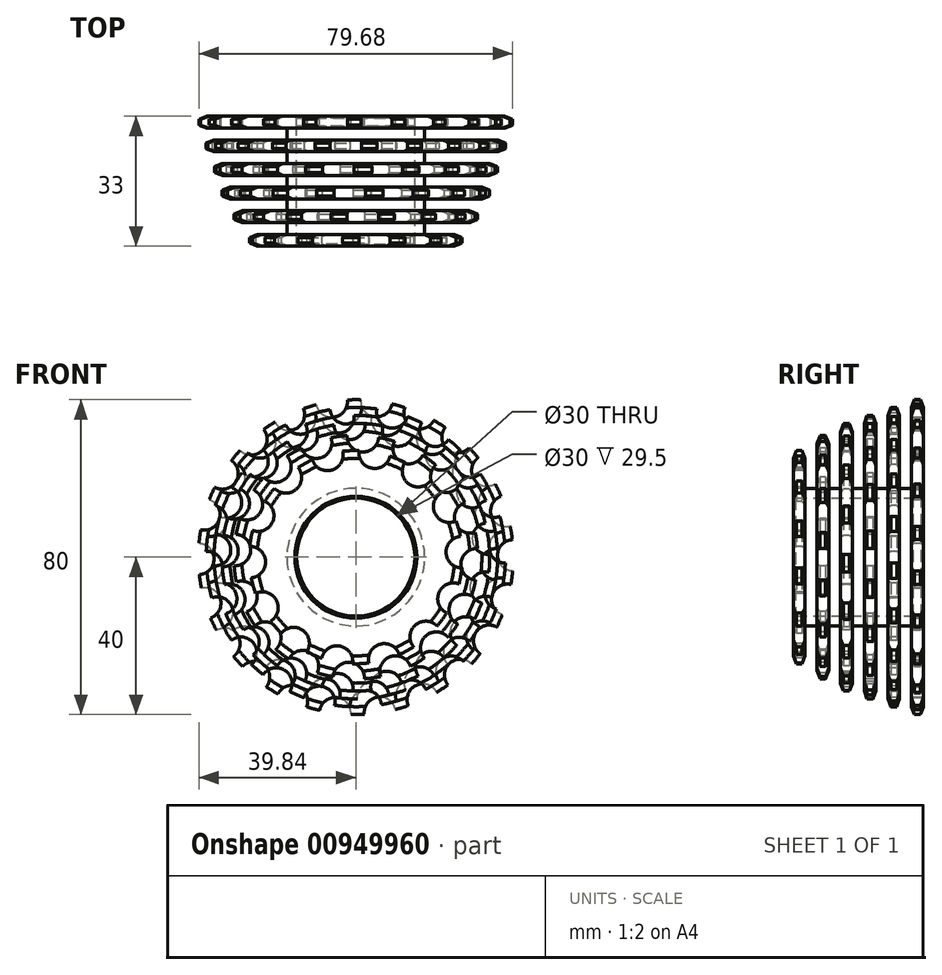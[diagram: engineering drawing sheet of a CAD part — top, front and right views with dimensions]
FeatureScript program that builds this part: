
annotation { "Feature Type Name" : "Feature", "Feature Type Description" : "" }
export const myFeature = defineFeature(function(context is Context, id is Id, definition is map)
    precondition{}
    {
        {
            var Q0;
            Q0=qCreatedBy(makeId("Front.planeOp"),FACE);
            var sketch = newSketch(context, id + "F0", { "sketchPlane" : qUnion([Q0])});
            skCircle(sketch, "E0", {"center": v(0, 0) * mm, "radius": 40 * mm});
            skCircle(sketch, "E1", {"center": v(-33.89, 21.25) * mm, "radius": 4 * mm});
            skCircle(sketch, "E2.1.0", {"center": v(-38.5, 10.85) * mm, "radius": 4 * mm});
            skCircle(sketch, "E2.2.0", {"center": v(-40, -0.44) * mm, "radius": 4 * mm});
            skCircle(sketch, "E2.3.0", {"center": v(-38.25, -11.7) * mm, "radius": 4 * mm});
            skCircle(sketch, "E2.4.0", {"center": v(-33.41, -22) * mm, "radius": 4 * mm});
            skCircle(sketch, "E2.5.0", {"center": v(-25.86, -30.52) * mm, "radius": 4 * mm});
            skCircle(sketch, "E2.6.0", {"center": v(-16.22, -36.57) * mm, "radius": 4 * mm});
            skCircle(sketch, "E2.7.0", {"center": v(-5.26, -39.65) * mm, "radius": 4 * mm});
            skCircle(sketch, "E2.8.0", {"center": v(6.13, -39.53) * mm, "radius": 4 * mm});
            skCircle(sketch, "E2.9.0", {"center": v(17.02, -36.2) * mm, "radius": 4 * mm});
            skCircle(sketch, "E2.10.0", {"center": v(26.53, -29.94) * mm, "radius": 4 * mm});
            skCircle(sketch, "E2.11.0", {"center": v(33.89, -21.25) * mm, "radius": 4 * mm});
            skCircle(sketch, "E2.12.0", {"center": v(38.5, -10.85) * mm, "radius": 4 * mm});
            skCircle(sketch, "E2.13.0", {"center": v(40, 0.44) * mm, "radius": 4 * mm});
            skCircle(sketch, "E2.14.0", {"center": v(38.25, 11.7) * mm, "radius": 4 * mm});
            skCircle(sketch, "E2.15.0", {"center": v(33.41, 22) * mm, "radius": 4 * mm});
            skCircle(sketch, "E2.16.0", {"center": v(25.86, 30.52) * mm, "radius": 4 * mm});
            skCircle(sketch, "E2.17.0", {"center": v(16.22, 36.57) * mm, "radius": 4 * mm});
            skCircle(sketch, "E2.18.0", {"center": v(5.26, 39.65) * mm, "radius": 4 * mm});
            skCircle(sketch, "E2.19.0", {"center": v(-6.13, 39.53) * mm, "radius": 4 * mm});
            skCircle(sketch, "E3", {"center": v(0, 0) * mm, "radius": 15 * mm});
            skCircle(sketch, "E4.1.20.0", {"center": v(-17.02, 36.2) * mm, "radius": 4 * mm});
            skCircle(sketch, "E4.1.21.0", {"center": v(-26.53, 29.94) * mm, "radius": 4 * mm});
            skSolve(sketch);
        }
        {
            var Q0;
            Q0=makeQuery(id+"F0.imprint","IMPRINT",FACE,{"disambiguationData":[TD([[makeQuery(id+"F0.imprint","IMPRINT",EDGE,{"derivedFrom":sQuery(id+"F0.wireOp",EDGE,"E0")}),1.0]])]});
            extrude(context, id + "F1", {"entities" : qUnion([Q0]), "depth" : 3 * mm, "offsetDistance" : 25 * mm});
        }
        {
            var Q0;
            {var subQ0=sQuery(id+"F0.wireOp",EDGE,"E0");Q0=makeQuery(id+"FjPS6zSCau8WYdw_1.boolean.opBoolean","SPLIT",EDGE,{"disambiguationData":[TD([makeQuery(id+"F1.opExtrude","SWEPT_FACE",FACE,{"disambiguationData":[OSD([subQ0])]}),makeQuery(id+"F1.opExtrude","CAP_FACE",FACE,{"disambiguationData":[OSD([subQ0])],"isStart":false}),makeQuery(id+"FjPS6zSCau8WYdw_1.opExtrude","SWEPT_FACE",FACE,{"disambiguationData":[OSD([sQuery(id+"FptURnvkRjZK9U8_1.wireOp",EDGE,"c81c12ed-b287-469f-bd1e-95274906ad68.5.0")])]}),makeQuery(id+"FjPS6zSCau8WYdw_1.opExtrude","SWEPT_FACE",FACE,{"disambiguationData":[OSD([sQuery(id+"FptURnvkRjZK9U8_1.wireOp",EDGE,"c81c12ed-b287-469f-bd1e-95274906ad68.6.0")])]})])],"derivedFrom":makeQuery(id+"F1.opExtrude","CAP_EDGE",EDGE,{"disambiguationData":[OSD([subQ0])],"isStart":false})});}
            chamfer(context, id + "F2", {"entities" : qUnion([Q0]), "chamferType" : ChamferType.TWO_OFFSETS, "width1" : 2 * mm, "oppositeDirection" : false, "width2" : 0.75 * mm, "tangentPropagation" : true});
        }
        {
            var Q0;
            {var subQ0=sQuery(id+"F0.wireOp",EDGE,"E0");Q0=makeQuery(id+"FjPS6zSCau8WYdw_1.boolean.opBoolean","SPLIT",EDGE,{"disambiguationData":[TD([makeQuery(id+"F1.opExtrude","SWEPT_FACE",FACE,{"disambiguationData":[OSD([subQ0])]}),makeQuery(id+"F1.opExtrude","CAP_FACE",FACE,{"disambiguationData":[OSD([subQ0])],"isStart":true}),makeQuery(id+"FjPS6zSCau8WYdw_1.opExtrude","SWEPT_FACE",FACE,{"disambiguationData":[OSD([sQuery(id+"FptURnvkRjZK9U8_1.wireOp",EDGE,"c81c12ed-b287-469f-bd1e-95274906ad68.21.0")])]}),makeQuery(id+"FjPS6zSCau8WYdw_1.opExtrude","SWEPT_FACE",FACE,{"disambiguationData":[OSD([sQuery(id+"FptURnvkRjZK9U8_1.wireOp",EDGE,"c81c12ed-b287-469f-bd1e-95274906ad68.22.0")])]})])],"derivedFrom":makeQuery(id+"F1.opExtrude","CAP_EDGE",EDGE,{"disambiguationData":[OSD([subQ0])],"isStart":true})});}
            chamfer(context, id + "F3", {"entities" : qUnion([Q0]), "chamferType" : ChamferType.TWO_OFFSETS, "width1" : 0.75 * mm, "oppositeDirection" : false, "width2" : 2 * mm, "tangentPropagation" : true});
        }
        {
            var Q0;
            Q0=makeQuery(id+"F1.opExtrude","CAP_EDGE",EDGE,{"disambiguationData":[OSD([sQuery(id+"F0.wireOp",EDGE,"E3")])],"isStart":false});
            var Q1;
            Q1=makeQuery(id+"F1.opExtrude","CAP_EDGE",EDGE,{"disambiguationData":[OSD([sQuery(id+"F0.wireOp",EDGE,"E3")])],"isStart":true});
            chamfer(context, id + "F4", {"entities" : qUnion([Q0, Q1]), "width" : 0.5 * mm, "tangentPropagation" : true});
        }
        {
            var Q0;
            Q0=makeQuery(id+"F1.opExtrude","CAP_FACE",FACE,{"disambiguationData":[OSD([sQuery(id+"F0.wireOp",EDGE,"E0"),sQuery(id+"F0.wireOp",EDGE,"E1"),sQuery(id+"F0.wireOp",EDGE,"E2.1.0"),sQuery(id+"F0.wireOp",EDGE,"E2.2.0"),sQuery(id+"F0.wireOp",EDGE,"E2.3.0"),sQuery(id+"F0.wireOp",EDGE,"E2.4.0"),sQuery(id+"F0.wireOp",EDGE,"E2.5.0"),sQuery(id+"F0.wireOp",EDGE,"E2.6.0"),sQuery(id+"F0.wireOp",EDGE,"E2.7.0"),sQuery(id+"F0.wireOp",EDGE,"E2.8.0"),sQuery(id+"F0.wireOp",EDGE,"E2.9.0"),sQuery(id+"F0.wireOp",EDGE,"E2.10.0"),sQuery(id+"F0.wireOp",EDGE,"E2.11.0"),sQuery(id+"F0.wireOp",EDGE,"E2.12.0"),sQuery(id+"F0.wireOp",EDGE,"E2.13.0"),sQuery(id+"F0.wireOp",EDGE,"E2.14.0"),sQuery(id+"F0.wireOp",EDGE,"E2.15.0"),sQuery(id+"F0.wireOp",EDGE,"E2.16.0"),sQuery(id+"F0.wireOp",EDGE,"E2.17.0"),sQuery(id+"F0.wireOp",EDGE,"E2.18.0"),sQuery(id+"F0.wireOp",EDGE,"E2.19.0"),sQuery(id+"F0.wireOp",EDGE,"E3"),sQuery(id+"F0.wireOp",EDGE,"E4.1.20.0"),sQuery(id+"F0.wireOp",EDGE,"E4.1.21.0")])],"isStart":false});
            var sketch = newSketch(context, id + "F5", { "sketchPlane" : qUnion([Q0])});
            skCircle(sketch, "E5", {"center": v(0, 0) * mm, "radius": 17.5 * mm});
            skSolve(sketch);
        }
        {
            var Q0;
            Q0 = qSketchRegion(id + "F5", true);
            extrude(context, id + "F6", {"entities" : qUnion([Q0]), "operationType" : NewBodyOperationType.ADD, "depth" : 3 * mm, "offsetDistance" : 25 * mm});
        }
        {
            var Q0;
            Q0=makeQuery(id+"F6.opExtrude","CAP_FACE",FACE,{"disambiguationData":[OSD([sQuery(id+"F5.wireOp",EDGE,"E5")])],"isStart":false});
            var sketch = newSketch(context, id + "F7", { "sketchPlane" : qUnion([Q0])});
            skCircle(sketch, "E6", {"center": v(0, 0) * mm, "radius": 38.02 * mm});
            skSolve(sketch);
        }
        {
            var Q0;
            Q0 = qSketchRegion(id + "F7", true);
            extrude(context, id + "F8", {"entities" : qUnion([Q0]), "operationType" : NewBodyOperationType.ADD, "depth" : 3 * mm, "offsetDistance" : 25 * mm});
        }
        {
            var Q0;
            Q0=makeQuery(id+"F8.opExtrude","CAP_EDGE",EDGE,{"disambiguationData":[OSD([sQuery(id+"F7.wireOp",EDGE,"E6")])],"isStart":false});
            var Q1;
            Q1=makeQuery(id+"F8.opExtrude","CAP_EDGE",EDGE,{"disambiguationData":[OSD([sQuery(id+"F7.wireOp",EDGE,"E6")])],"isStart":true});
            chamfer(context, id + "F9", {"entities" : qUnion([Q0, Q1]), "chamferType" : ChamferType.TWO_OFFSETS, "width1" : 2 * mm, "oppositeDirection" : false, "width2" : 0.75 * mm, "tangentPropagation" : true});
        }
        {
            var Q0;
            Q0=makeQuery(id+"F8.opExtrude","CAP_FACE",FACE,{"disambiguationData":[OSD([sQuery(id+"F7.wireOp",EDGE,"E6")])],"isStart":false});
            var sketch = newSketch(context, id + "F10", { "sketchPlane" : qUnion([Q0])});
            skCircle(sketch, "E7", {"center": v(-32.1, 20.2) * mm, "radius": 4 * mm});
            skCircle(sketch, "E8.1.0", {"center": v(-36.78, 9.29) * mm, "radius": 4 * mm});
            skCircle(sketch, "E8.2.0", {"center": v(-37.85, -2.53) * mm, "radius": 4 * mm});
            skCircle(sketch, "E8.3.0", {"center": v(-35.21, -14.1) * mm, "radius": 4 * mm});
            skCircle(sketch, "E8.4.0", {"center": v(-29.13, -24.3) * mm, "radius": 4 * mm});
            skCircle(sketch, "E8.5.0", {"center": v(-20.2, -32.1) * mm, "radius": 4 * mm});
            skCircle(sketch, "E8.6.0", {"center": v(-9.29, -36.78) * mm, "radius": 4 * mm});
            skCircle(sketch, "E8.7.0", {"center": v(2.53, -37.85) * mm, "radius": 4 * mm});
            skCircle(sketch, "E8.8.0", {"center": v(14.1, -35.21) * mm, "radius": 4 * mm});
            skCircle(sketch, "E8.9.0", {"center": v(24.3, -29.13) * mm, "radius": 4 * mm});
            skCircle(sketch, "E8.10.0", {"center": v(32.1, -20.2) * mm, "radius": 4 * mm});
            skCircle(sketch, "E8.11.0", {"center": v(36.78, -9.29) * mm, "radius": 4 * mm});
            skCircle(sketch, "E8.12.0", {"center": v(37.85, 2.53) * mm, "radius": 4 * mm});
            skCircle(sketch, "E8.13.0", {"center": v(35.21, 14.1) * mm, "radius": 4 * mm});
            skCircle(sketch, "E8.14.0", {"center": v(29.13, 24.3) * mm, "radius": 4 * mm});
            skCircle(sketch, "E8.15.0", {"center": v(20.2, 32.1) * mm, "radius": 4 * mm});
            skCircle(sketch, "E8.16.0", {"center": v(9.29, 36.78) * mm, "radius": 4 * mm});
            skCircle(sketch, "E8.17.0", {"center": v(-2.53, 37.85) * mm, "radius": 4 * mm});
            skCircle(sketch, "E8.18.0", {"center": v(-14.1, 35.21) * mm, "radius": 4 * mm});
            skCircle(sketch, "E8.19.0", {"center": v(-24.3, 29.13) * mm, "radius": 4 * mm});
            skPoint(sketch, "E8.center", {"position": v(0, 0) * mm});
            skSolve(sketch);
        }
        {
            var Q0;
            Q0 = qSketchRegion(id + "F10", true);
            extrude(context, id + "F11", {"entities" : qUnion([Q0]), "operationType" : NewBodyOperationType.REMOVE, "oppositeDirection" : true, "depth" : 3 * mm, "offsetDistance" : 25 * mm});
        }
        {
            var Q0;
            Q0=makeQuery(id+"F8.opExtrude","CAP_FACE",FACE,{"disambiguationData":[OSD([sQuery(id+"F7.wireOp",EDGE,"E6")])],"isStart":false});
            var sketch = newSketch(context, id + "F12", { "sketchPlane" : qUnion([Q0])});
            skCircle(sketch, "E9", {"center": v(0, 0) * mm, "radius": 17.5 * mm});
            skSolve(sketch);
        }
        {
            var Q0;
            Q0 = qSketchRegion(id + "F12", true);
            extrude(context, id + "F13", {"entities" : qUnion([Q0]), "operationType" : NewBodyOperationType.ADD, "depth" : 3 * mm, "offsetDistance" : 25 * mm});
        }
        {
            var Q0;
            Q0=makeQuery(id+"F13.opExtrude","CAP_FACE",FACE,{"disambiguationData":[OSD([sQuery(id+"F12.wireOp",EDGE,"E9")])],"isStart":false});
            var sketch = newSketch(context, id + "F14", { "sketchPlane" : qUnion([Q0])});
            skCircle(sketch, "E10", {"center": v(0, 0) * mm, "radius": 36 * mm});
            skSolve(sketch);
        }
        {
            var Q0;
            Q0 = qSketchRegion(id + "F14", true);
            extrude(context, id + "F15", {"entities" : qUnion([Q0]), "operationType" : NewBodyOperationType.ADD, "depth" : 3 * mm, "offsetDistance" : 25 * mm});
        }
        {
            var Q0;
            Q0=makeQuery(id+"F15.opExtrude","CAP_FACE",FACE,{"disambiguationData":[OSD([sQuery(id+"F14.wireOp",EDGE,"E10")])],"isStart":false});
            var Q1;
            Q1=makeQuery(id+"F15.opExtrude","CAP_EDGE",EDGE,{"disambiguationData":[OSD([sQuery(id+"F14.wireOp",EDGE,"E10")])],"isStart":true});
            chamfer(context, id + "F16", {"entities" : qUnion([Q0, Q1]), "chamferType" : ChamferType.TWO_OFFSETS, "width1" : 2 * mm, "oppositeDirection" : false, "width2" : .75 * mm, "tangentPropagation" : true});
        }
        {
            var Q0;
            Q0=makeQuery(id+"F15.opExtrude","CAP_FACE",FACE,{"disambiguationData":[OSD([sQuery(id+"F14.wireOp",EDGE,"E10")])],"isStart":false});
            var sketch = newSketch(context, id + "F17", { "sketchPlane" : qUnion([Q0])});
            skCircle(sketch, "E11", {"center": v(-26.24, 24.36) * mm, "radius": 4 * mm});
            skCircle(sketch, "E12.1.0", {"center": v(-32.99, 13.92) * mm, "radius": 4 * mm});
            skCircle(sketch, "E12.2.0", {"center": v(-35.76, 1.8) * mm, "radius": 4 * mm});
            skCircle(sketch, "E12.3.0", {"center": v(-34.22, -10.54) * mm, "radius": 4 * mm});
            skCircle(sketch, "E12.4.0", {"center": v(-28.55, -21.6) * mm, "radius": 4 * mm});
            skCircle(sketch, "E12.5.0", {"center": v(-19.43, -30.07) * mm, "radius": 4 * mm});
            skCircle(sketch, "E12.6.0", {"center": v(-7.98, -34.9) * mm, "radius": 4 * mm});
            skCircle(sketch, "E12.7.0", {"center": v(4.44, -35.53) * mm, "radius": 4 * mm});
            skCircle(sketch, "E12.8.0", {"center": v(16.32, -31.87) * mm, "radius": 4 * mm});
            skCircle(sketch, "E12.9.0", {"center": v(26.24, -24.36) * mm, "radius": 4 * mm});
            skCircle(sketch, "E12.10.0", {"center": v(32.99, -13.92) * mm, "radius": 4 * mm});
            skCircle(sketch, "E12.11.0", {"center": v(35.76, -1.8) * mm, "radius": 4 * mm});
            skCircle(sketch, "E12.12.0", {"center": v(34.22, 10.54) * mm, "radius": 4 * mm});
            skCircle(sketch, "E12.13.0", {"center": v(28.55, 21.6) * mm, "radius": 4 * mm});
            skCircle(sketch, "E12.14.0", {"center": v(19.43, 30.07) * mm, "radius": 4 * mm});
            skCircle(sketch, "E12.15.0", {"center": v(7.98, 34.9) * mm, "radius": 4 * mm});
            skCircle(sketch, "E12.16.0", {"center": v(-4.44, 35.53) * mm, "radius": 4 * mm});
            skCircle(sketch, "E12.17.0", {"center": v(-16.32, 31.87) * mm, "radius": 4 * mm});
            skPoint(sketch, "E12.center", {"position": v(0, 0) * mm});
            skSolve(sketch);
        }
        {
            var Q0;
            Q0 = qSketchRegion(id + "F17", true);
            extrude(context, id + "F18", {"entities" : qUnion([Q0]), "operationType" : NewBodyOperationType.REMOVE, "oppositeDirection" : true, "depth" : 3 * mm, "offsetDistance" : 25 * mm});
        }
        {
            var Q0;
            Q0=makeQuery(id+"F15.opExtrude","CAP_FACE",FACE,{"disambiguationData":[OSD([sQuery(id+"F14.wireOp",EDGE,"E10")])],"isStart":false});
            var sketch = newSketch(context, id + "F19", { "sketchPlane" : qUnion([Q0])});
            skCircle(sketch, "E13", {"center": v(0, 0) * mm, "radius": 17.5 * mm});
            skSolve(sketch);
        }
        {
            var Q0;
            Q0 = qSketchRegion(id + "F19", true);
            extrude(context, id + "F20", {"entities" : qUnion([Q0]), "operationType" : NewBodyOperationType.ADD, "depth" : 3 * mm, "offsetDistance" : 25 * mm});
        }
        {
            var Q0;
            Q0=makeQuery(id+"F20.opExtrude","CAP_FACE",FACE,{"disambiguationData":[OSD([sQuery(id+"F19.wireOp",EDGE,"E13")])],"isStart":false});
            var sketch = newSketch(context, id + "F21", { "sketchPlane" : qUnion([Q0])});
            skCircle(sketch, "E14", {"center": v(0, 0) * mm, "radius": 34.02 * mm});
            skSolve(sketch);
        }
        {
            var Q0;
            Q0 = qSketchRegion(id + "F21", true);
            extrude(context, id + "F22", {"entities" : qUnion([Q0]), "operationType" : NewBodyOperationType.ADD, "depth" : 3 * mm, "offsetDistance" : 25 * mm});
        }
        {
            var Q0;
            Q0=makeQuery(id+"F22.opExtrude","CAP_FACE",FACE,{"disambiguationData":[OSD([sQuery(id+"F21.wireOp",EDGE,"E14")])],"isStart":false});
            var Q1;
            Q1=makeQuery(id+"F22.opExtrude","CAP_EDGE",EDGE,{"disambiguationData":[OSD([sQuery(id+"F21.wireOp",EDGE,"E14")])],"isStart":true});
            chamfer(context, id + "F23", {"entities" : qUnion([Q0, Q1]), "chamferType" : ChamferType.TWO_OFFSETS, "width1" : 2 * mm, "oppositeDirection" : false, "width2" : 0.75 * mm, "tangentPropagation" : true});
        }
        {
            var Q0;
            Q0=makeQuery(id+"F22.opExtrude","CAP_FACE",FACE,{"disambiguationData":[OSD([sQuery(id+"F21.wireOp",EDGE,"E14")])],"isStart":false});
            var sketch = newSketch(context, id + "F24", { "sketchPlane" : qUnion([Q0])});
            skCircle(sketch, "E15", {"center": v(-23.99, 23.95) * mm, "radius": 4 * mm});
            skCircle(sketch, "E16.1.0", {"center": v(-31.02, 13.67) * mm, "radius": 4 * mm});
            skCircle(sketch, "E16.2.0", {"center": v(-33.86, 1.54) * mm, "radius": 4 * mm});
            skCircle(sketch, "E16.3.0", {"center": v(-32.13, -10.8) * mm, "radius": 4 * mm});
            skCircle(sketch, "E16.4.0", {"center": v(-26.06, -21.67) * mm, "radius": 4 * mm});
            skCircle(sketch, "E16.5.0", {"center": v(-16.47, -29.62) * mm, "radius": 4 * mm});
            skCircle(sketch, "E16.6.0", {"center": v(-4.66, -33.57) * mm, "radius": 4 * mm});
            skCircle(sketch, "E16.7.0", {"center": v(7.78, -33) * mm, "radius": 4 * mm});
            skCircle(sketch, "E16.8.0", {"center": v(19.18, -27.95) * mm, "radius": 4 * mm});
            skCircle(sketch, "E16.9.0", {"center": v(27.98, -19.14) * mm, "radius": 4 * mm});
            skCircle(sketch, "E16.10.0", {"center": v(33, -7.74) * mm, "radius": 4 * mm});
            skCircle(sketch, "E16.11.0", {"center": v(33.57, 4.7) * mm, "radius": 4 * mm});
            skCircle(sketch, "E16.12.0", {"center": v(29.6, 16.52) * mm, "radius": 4 * mm});
            skCircle(sketch, "E16.13.0", {"center": v(21.64, 26.1) * mm, "radius": 4 * mm});
            skCircle(sketch, "E16.14.0", {"center": v(10.75, 32.15) * mm, "radius": 4 * mm});
            skCircle(sketch, "E16.15.0", {"center": v(-1.59, 33.86) * mm, "radius": 4 * mm});
            skCircle(sketch, "E16.16.0", {"center": v(-13.71, 31) * mm, "radius": 4 * mm});
            skPoint(sketch, "E16.center", {"position": v(0, 0) * mm});
            skSolve(sketch);
        }
        {
            var Q0;
            Q0 = qSketchRegion(id + "F24", true);
            extrude(context, id + "F25", {"entities" : qUnion([Q0]), "operationType" : NewBodyOperationType.REMOVE, "oppositeDirection" : true, "depth" : 3 * mm, "offsetDistance" : 25 * mm});
        }
        {
            var Q0;
            Q0=makeQuery(id+"F22.opExtrude","CAP_FACE",FACE,{"disambiguationData":[OSD([sQuery(id+"F21.wireOp",EDGE,"E14")])],"isStart":false});
            var sketch = newSketch(context, id + "F26", { "sketchPlane" : qUnion([Q0])});
            skCircle(sketch, "E17", {"center": v(0, 0) * mm, "radius": 17.5 * mm});
            skSolve(sketch);
        }
        {
            var Q0;
            Q0 = qSketchRegion(id + "F26", true);
            extrude(context, id + "F27", {"entities" : qUnion([Q0]), "operationType" : NewBodyOperationType.ADD, "depth" : 3 * mm, "offsetDistance" : 25 * mm});
        }
        {
            var Q0;
            Q0=makeQuery(id+"F27.opExtrude","CAP_FACE",FACE,{"disambiguationData":[OSD([sQuery(id+"F26.wireOp",EDGE,"E17")])],"isStart":false});
            var sketch = newSketch(context, id + "F28", { "sketchPlane" : qUnion([Q0])});
            skCircle(sketch, "E18", {"center": v(0, 0) * mm, "radius": 30.98 * mm});
            skSolve(sketch);
        }
        {
            var Q0;
            Q0 = qSketchRegion(id + "F28", true);
            extrude(context, id + "F29", {"entities" : qUnion([Q0]), "operationType" : NewBodyOperationType.ADD, "depth" : 3 * mm, "offsetDistance" : 25 * mm});
        }
        {
            var Q0;
            Q0=makeQuery(id+"F29.opExtrude","CAP_EDGE",EDGE,{"disambiguationData":[OSD([sQuery(id+"F28.wireOp",EDGE,"E18")])],"isStart":false});
            var Q1;
            Q1=makeQuery(id+"F29.opExtrude","CAP_EDGE",EDGE,{"disambiguationData":[OSD([sQuery(id+"F28.wireOp",EDGE,"E18")])],"isStart":true});
            chamfer(context, id + "F30", {"entities" : qUnion([Q0, Q1]), "chamferType" : ChamferType.TWO_OFFSETS, "width1" : 2 * mm, "oppositeDirection" : false, "width2" : 0.8 * mm, "tangentPropagation" : true});
        }
        {
            var Q0;
            Q0=makeQuery(id+"F29.opExtrude","CAP_FACE",FACE,{"disambiguationData":[OSD([sQuery(id+"F28.wireOp",EDGE,"E18")])],"isStart":false});
            var sketch = newSketch(context, id + "F31", { "sketchPlane" : qUnion([Q0])});
            skCircle(sketch, "E19", {"center": v(-20.44, 23) * mm, "radius": 4 * mm});
            skCircle(sketch, "E20.1.0", {"center": v(-27.68, 13.42) * mm, "radius": 4 * mm});
            skCircle(sketch, "E20.2.0", {"center": v(-30.71, 1.8) * mm, "radius": 4 * mm});
            skCircle(sketch, "E20.3.0", {"center": v(-29.07, -10.08) * mm, "radius": 4 * mm});
            skCircle(sketch, "E20.4.0", {"center": v(-23, -20.44) * mm, "radius": 4 * mm});
            skCircle(sketch, "E20.5.0", {"center": v(-13.42, -27.68) * mm, "radius": 4 * mm});
            skCircle(sketch, "E20.6.0", {"center": v(-1.8, -30.71) * mm, "radius": 4 * mm});
            skCircle(sketch, "E20.7.0", {"center": v(10.08, -29.07) * mm, "radius": 4 * mm});
            skCircle(sketch, "E20.8.0", {"center": v(20.44, -23) * mm, "radius": 4 * mm});
            skCircle(sketch, "E20.9.0", {"center": v(27.68, -13.42) * mm, "radius": 4 * mm});
            skCircle(sketch, "E20.10.0", {"center": v(30.71, -1.8) * mm, "radius": 4 * mm});
            skCircle(sketch, "E20.11.0", {"center": v(29.07, 10.08) * mm, "radius": 4 * mm});
            skCircle(sketch, "E20.12.0", {"center": v(23, 20.44) * mm, "radius": 4 * mm});
            skCircle(sketch, "E20.13.0", {"center": v(13.42, 27.68) * mm, "radius": 4 * mm});
            skCircle(sketch, "E20.14.0", {"center": v(1.8, 30.71) * mm, "radius": 4 * mm});
            skCircle(sketch, "E20.15.0", {"center": v(-10.08, 29.07) * mm, "radius": 4 * mm});
            skPoint(sketch, "E20.center", {"position": v(0, 0) * mm});
            skSolve(sketch);
        }
        {
            var Q0;
            Q0 = qSketchRegion(id + "F31", true);
            extrude(context, id + "F32", {"entities" : qUnion([Q0]), "operationType" : NewBodyOperationType.REMOVE, "oppositeDirection" : true, "depth" : 3 * mm, "offsetDistance" : 25 * mm});
        }
        {
            var Q0;
            Q0=makeQuery(id+"F29.opExtrude","CAP_FACE",FACE,{"disambiguationData":[OSD([sQuery(id+"F28.wireOp",EDGE,"E18")])],"isStart":false});
            var sketch = newSketch(context, id + "F33", { "sketchPlane" : qUnion([Q0])});
            skCircle(sketch, "E21", {"center": v(0, 0) * mm, "radius": 17.5 * mm});
            skSolve(sketch);
        }
        {
            var Q0;
            Q0 = qSketchRegion(id + "F33", true);
            extrude(context, id + "F34", {"entities" : qUnion([Q0]), "operationType" : NewBodyOperationType.ADD, "depth" : 3 * mm, "offsetDistance" : 25 * mm});
        }
        {
            var Q0;
            Q0=makeQuery(id+"F34.opExtrude","CAP_FACE",FACE,{"disambiguationData":[OSD([sQuery(id+"F33.wireOp",EDGE,"E21")])],"isStart":false});
            var sketch = newSketch(context, id + "F35", { "sketchPlane" : qUnion([Q0])});
            skCircle(sketch, "E22", {"center": v(0, 0) * mm, "radius": 27.08 * mm});
            skSolve(sketch);
        }
        {
            var Q0;
            Q0 = qSketchRegion(id + "F35", true);
            extrude(context, id + "F36", {"entities" : qUnion([Q0]), "operationType" : NewBodyOperationType.ADD, "depth" : 3 * mm, "offsetDistance" : 25 * mm});
        }
        {
            var Q0;
            Q0=makeQuery(id+"F36.opExtrude","CAP_EDGE",EDGE,{"disambiguationData":[OSD([sQuery(id+"F35.wireOp",EDGE,"E22")])],"isStart":false});
            var Q1;
            Q1=makeQuery(id+"F36.opExtrude","CAP_EDGE",EDGE,{"disambiguationData":[OSD([sQuery(id+"F35.wireOp",EDGE,"E22")])],"isStart":true});
            chamfer(context, id + "F37", {"entities" : qUnion([Q0, Q1]), "chamferType" : ChamferType.TWO_OFFSETS, "width1" : 2 * mm, "oppositeDirection" : false, "width2" : 0.8 * mm, "tangentPropagation" : true});
        }
        {
            var Q0;
            Q0=makeQuery(id+"F36.opExtrude","CAP_FACE",FACE,{"disambiguationData":[OSD([sQuery(id+"F35.wireOp",EDGE,"E22")])],"isStart":false});
            var sketch = newSketch(context, id + "F38", { "sketchPlane" : qUnion([Q0])});
            skCircle(sketch, "E23", {"center": v(-17.78, 20.27) * mm, "radius": 4 * mm});
            skCircle(sketch, "E24.1.0", {"center": v(-24.8, 10.55) * mm, "radius": 4 * mm});
            skCircle(sketch, "E24.2.0", {"center": v(-26.93, -1.26) * mm, "radius": 4 * mm});
            skCircle(sketch, "E24.3.0", {"center": v(-23.71, -12.82) * mm, "radius": 4 * mm});
            skCircle(sketch, "E24.4.0", {"center": v(-15.8, -21.84) * mm, "radius": 4 * mm});
            skCircle(sketch, "E24.5.0", {"center": v(-4.76, -26.53) * mm, "radius": 4 * mm});
            skCircle(sketch, "E24.6.0", {"center": v(7.22, -25.97) * mm, "radius": 4 * mm});
            skCircle(sketch, "E24.7.0", {"center": v(17.78, -20.27) * mm, "radius": 4 * mm});
            skCircle(sketch, "E24.8.0", {"center": v(24.8, -10.55) * mm, "radius": 4 * mm});
            skCircle(sketch, "E24.9.0", {"center": v(26.93, 1.26) * mm, "radius": 4 * mm});
            skCircle(sketch, "E24.10.0", {"center": v(23.71, 12.82) * mm, "radius": 4 * mm});
            skCircle(sketch, "E24.11.0", {"center": v(15.8, 21.84) * mm, "radius": 4 * mm});
            skCircle(sketch, "E24.12.0", {"center": v(4.76, 26.53) * mm, "radius": 4 * mm});
            skCircle(sketch, "E24.13.0", {"center": v(-7.22, 25.97) * mm, "radius": 4 * mm});
            skPoint(sketch, "E24.center", {"position": v(0, 0) * mm});
            skSolve(sketch);
        }
        {
            var Q0;
            Q0 = qSketchRegion(id + "F38", true);
            extrude(context, id + "F39", {"entities" : qUnion([Q0]), "operationType" : NewBodyOperationType.REMOVE, "oppositeDirection" : true, "depth" : 3 * mm, "offsetDistance" : 25 * mm});
        }
        {
            var Q0;
            Q0=makeQuery(id+"F6.opExtrude","CAP_FACE",FACE,{"disambiguationData":[OSD([sQuery(id+"F5.wireOp",EDGE,"E5")])],"isStart":true});
            var sketch = newSketch(context, id + "F40", { "sketchPlane" : qUnion([Q0])});
            skCircle(sketch, "E25", {"center": v(0, 0) * mm, "radius": 15 * mm});
            skSolve(sketch);
        }
        {
            var Q0;
            Q0 = qSketchRegion(id + "F40", true);
            extrude(context, id + "F41", {"entities" : qUnion([Q0]), "operationType" : NewBodyOperationType.REMOVE, "endBound" : BoundingType.THROUGH_ALL, "oppositeDirection" : true, "depth" : 25 * mm, "offsetDistance" : 25 * mm});
        }
        {
            var Q0;
            Q0=makeQuery(id+"F41.boolean.opBoolean","INTERSECT",EDGE,{"derivedFrom":[makeQuery(id+"F36.opExtrude","CAP_FACE",FACE,{"disambiguationData":[OSD([sQuery(id+"F35.wireOp",EDGE,"E22")])],"isStart":false}),makeQuery(id+"F41.opExtrude","SWEPT_FACE",FACE,{"disambiguationData":[OSD([sQuery(id+"F40.wireOp",EDGE,"E25")])]})]});
            chamfer(context, id + "F42", {"entities" : qUnion([Q0]), "width" : 0.5 * mm, "tangentPropagation" : true});
        }
    });
